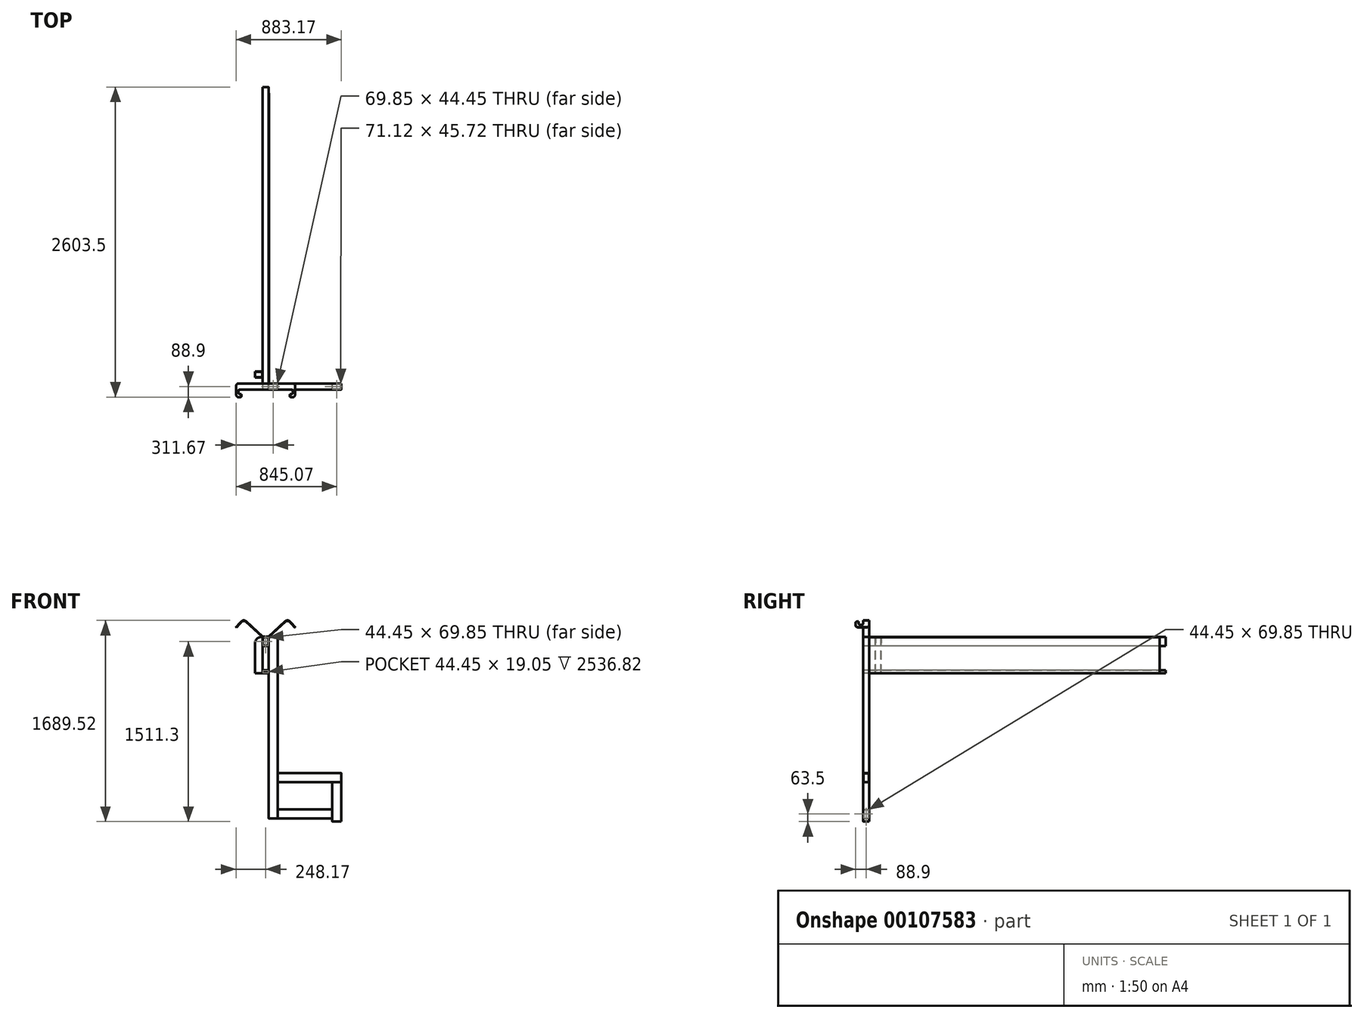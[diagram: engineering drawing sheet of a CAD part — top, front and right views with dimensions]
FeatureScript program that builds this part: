
annotation { "Feature Type Name" : "Feature", "Feature Type Description" : "" }
export const myFeature = defineFeature(function(context is Context, id is Id, definition is map)
    precondition{}
    {
        {
            var Q0;
            Q0=qCreatedBy(makeId("Right.planeOp"),FACE);
            var sketch = newSketch(context, id + "F0", { "sketchPlane" : qUnion([Q0])});
            skLineSegment(sketch, "E0.bottom", {"start": v(-25.4, 38.1) * mm, "end": v(25.4, 38.1) * mm});
            skLineSegment(sketch, "E0.top", {"start": v(-25.4, -38.1) * mm, "end": v(25.4, -38.1) * mm});
            skLineSegment(sketch, "E0.left", {"start": v(-25.4, 38.1) * mm, "end": v(-25.4, -38.1) * mm});
            skLineSegment(sketch, "E0.right", {"start": v(25.4, 38.1) * mm, "end": v(25.4, -38.1) * mm});
            skLineSegment(sketch, "E1", {"start": v(25.4, 38.1) * mm, "end": v(-25.4, -38.1) * mm, "construction": true});
            skSolve(sketch);
        }
        {
            var Q0;
            Q0=makeQuery(id+"F0.imprint","IMPRINT",FACE,{"disambiguationData":[TD([[makeQuery(id+"F0.imprint","IMPRINT",EDGE,{"derivedFrom":sQuery(id+"F0.wireOp",EDGE,"E0.bottom")}),-1.0]])]});
            extrude(context, id + "F1", {"entities" : qUnion([Q0]), "endBound" : BoundingType.SYMMETRIC, "depth" : 457.2 * mm});
        }
        {
            var Q0;
            Q0=makeQuery(id+"F1.opExtrude","SWEPT_EDGE",EDGE,{"disambiguationData":[OSD([sQuery(id+"F0.wireOp",EDGE,"E0.bottom"),sQuery(id+"F0.wireOp",EDGE,"E0.left")])]});
            var Q1;
            Q1=makeQuery(id+"F1.opExtrude","SWEPT_EDGE",EDGE,{"disambiguationData":[OSD([sQuery(id+"F0.wireOp",EDGE,"E0.bottom"),sQuery(id+"F0.wireOp",EDGE,"E0.right")])]});
            var Q2;
            Q2=makeQuery(id+"F1.opExtrude","SWEPT_EDGE",EDGE,{"disambiguationData":[OSD([sQuery(id+"F0.wireOp",EDGE,"E0.top"),sQuery(id+"F0.wireOp",EDGE,"E0.left")])]});
            var Q3;
            Q3=makeQuery(id+"F1.opExtrude","SWEPT_EDGE",EDGE,{"disambiguationData":[OSD([sQuery(id+"F0.wireOp",EDGE,"E0.top"),sQuery(id+"F0.wireOp",EDGE,"E0.right")])]});
            fillet(context, id + "F2", {"entities" : qUnion([Q0, Q1, Q2, Q3]), "radius" : 2.4 * mm, "tangentPropagation" : true, "allowEdgeOverflow" : false});
        }
        {
            var Q0;
            Q0=makeQuery(id+"F1.opExtrude","CAP_FACE",FACE,{"disambiguationData":[OSD([sQuery(id+"F0.wireOp",EDGE,"E0.bottom"),sQuery(id+"F0.wireOp",EDGE,"E0.top"),sQuery(id+"F0.wireOp",EDGE,"E0.left"),sQuery(id+"F0.wireOp",EDGE,"E0.right")])],"isStart":false});
            var Q1;
            Q1=makeQuery(id+"F1.opExtrude","CAP_FACE",FACE,{"disambiguationData":[OSD([sQuery(id+"F0.wireOp",EDGE,"E0.bottom"),sQuery(id+"F0.wireOp",EDGE,"E0.top"),sQuery(id+"F0.wireOp",EDGE,"E0.left"),sQuery(id+"F0.wireOp",EDGE,"E0.right")])],"isStart":true});
            shell(context, id + "F3", {"entities" : qUnion([Q0, Q1]), "thickness" : 3.17 * mm});
        }
        {
            var Q0;
            Q0=makeQuery(id+"F1.opExtrude","SWEPT_FACE",FACE,{"disambiguationData":[OSD([sQuery(id+"F0.wireOp",EDGE,"E0.top")])]});
            var sketch = newSketch(context, id + "F4", { "sketchPlane" : qUnion([Q0])});
            skLineSegment(sketch, "E2.bottom", {"start": v(-304.8, 25.4) * mm, "end": v(-228.6, 25.4) * mm});
            skLineSegment(sketch, "E2.top", {"start": v(-304.8, -25.4) * mm, "end": v(-228.6, -25.4) * mm});
            skLineSegment(sketch, "E2.left", {"start": v(-304.8, 25.4) * mm, "end": v(-304.8, -25.4) * mm});
            skLineSegment(sketch, "E2.right", {"start": v(-228.6, 25.4) * mm, "end": v(-228.6, -25.4) * mm});
            skSolve(sketch);
        }
        {
            var Q0;
            Q0 = qSketchRegion(id + "F4", true);
            extrude(context, id + "F5", {"entities" : qUnion([Q0]), "oppositeDirection" : true, "depth" : 1524 * mm});
        }
        {
            var Q0;
            Q0=makeQuery(id+"F5.opExtrude","SWEPT_EDGE",EDGE,{"disambiguationData":[OSD([sQuery(id+"F4.wireOp",EDGE,"E2.bottom"),sQuery(id+"F4.wireOp",EDGE,"E2.right")])]});
            var Q1;
            Q1=makeQuery(id+"F5.opExtrude","SWEPT_EDGE",EDGE,{"disambiguationData":[OSD([sQuery(id+"F4.wireOp",EDGE,"E2.top"),sQuery(id+"F4.wireOp",EDGE,"E2.right")])]});
            var Q2;
            Q2=makeQuery(id+"F5.opExtrude","SWEPT_EDGE",EDGE,{"disambiguationData":[OSD([sQuery(id+"F4.wireOp",EDGE,"E2.bottom"),sQuery(id+"F4.wireOp",EDGE,"E2.left")])]});
            var Q3;
            Q3=makeQuery(id+"F5.opExtrude","SWEPT_EDGE",EDGE,{"disambiguationData":[OSD([sQuery(id+"F4.wireOp",EDGE,"E2.top"),sQuery(id+"F4.wireOp",EDGE,"E2.left")])]});
            fillet(context, id + "F6", {"entities" : qUnion([Q0, Q1, Q2, Q3]), "radius" : 2.4 * mm, "tangentPropagation" : true, "allowEdgeOverflow" : false});
        }
        {
            var Q0;
            Q0=makeQuery(id+"F5.opExtrude","CAP_FACE",FACE,{"disambiguationData":[OSD([sQuery(id+"F4.wireOp",EDGE,"E2.bottom"),sQuery(id+"F4.wireOp",EDGE,"E2.top"),sQuery(id+"F4.wireOp",EDGE,"E2.left"),sQuery(id+"F4.wireOp",EDGE,"E2.right")])],"isStart":false});
            var Q1;
            Q1=makeQuery(id+"F5.opExtrude","CAP_FACE",FACE,{"disambiguationData":[OSD([sQuery(id+"F4.wireOp",EDGE,"E2.bottom"),sQuery(id+"F4.wireOp",EDGE,"E2.top"),sQuery(id+"F4.wireOp",EDGE,"E2.left"),sQuery(id+"F4.wireOp",EDGE,"E2.right")])],"isStart":true});
            shell(context, id + "F7", {"entities" : qUnion([Q0, Q1]), "thickness" : 3.17 * mm});
        }
        {
            var Q0;
            Q0=makeQuery(id+"F5.opExtrude","SWEPT_FACE",FACE,{"disambiguationData":[OSD([sQuery(id+"F4.wireOp",EDGE,"E2.bottom")])]});
            var sketch = newSketch(context, id + "F8", { "sketchPlane" : qUnion([Q0])});
            skLineSegment(sketch, "E3.bottom", {"start": v(-355.6, 1485.9) * mm, "end": v(-304.8, 1485.9) * mm});
            skLineSegment(sketch, "E3.top", {"start": v(-355.6, 1409.7) * mm, "end": v(-304.8, 1409.7) * mm});
            skLineSegment(sketch, "E3.left", {"start": v(-355.6, 1485.9) * mm, "end": v(-355.6, 1409.7) * mm});
            skLineSegment(sketch, "E3.right", {"start": v(-304.8, 1485.9) * mm, "end": v(-304.8, 1409.7) * mm});
            skSolve(sketch);
        }
        {
            var Q0;
            Q0=makeQuery(id+"F8.imprint","IMPRINT",FACE,{"disambiguationData":[TD([[makeQuery(id+"F8.imprint","IMPRINT",EDGE,{"derivedFrom":sQuery(id+"F8.wireOp",EDGE,"E3.bottom")}),-1.0]])]});
            extrude(context, id + "F9", {"entities" : qUnion([Q0]), "oppositeDirection" : true, "depth" : 2540 * mm});
        }
        {
            var Q0;
            Q0=makeQuery(id+"F9.opExtrude","SWEPT_EDGE",EDGE,{"disambiguationData":[OSD([sQuery(id+"F8.wireOp",EDGE,"E3.bottom"),sQuery(id+"F8.wireOp",EDGE,"E3.right")])]});
            var Q1;
            Q1=makeQuery(id+"F9.opExtrude","SWEPT_EDGE",EDGE,{"disambiguationData":[OSD([sQuery(id+"F8.wireOp",EDGE,"E3.bottom"),sQuery(id+"F8.wireOp",EDGE,"E3.left")])]});
            var Q2;
            Q2=makeQuery(id+"F9.opExtrude","SWEPT_EDGE",EDGE,{"disambiguationData":[OSD([sQuery(id+"F8.wireOp",EDGE,"E3.top"),sQuery(id+"F8.wireOp",EDGE,"E3.right")])]});
            var Q3;
            Q3=makeQuery(id+"F9.opExtrude","SWEPT_EDGE",EDGE,{"disambiguationData":[OSD([sQuery(id+"F8.wireOp",EDGE,"E3.top"),sQuery(id+"F8.wireOp",EDGE,"E3.left")])]});
            fillet(context, id + "F10", {"entities" : qUnion([Q0, Q1, Q2, Q3]), "radius" : 2.4 * mm, "tangentPropagation" : true, "allowEdgeOverflow" : false});
        }
        {
            var Q0;
            Q0=makeQuery(id+"F9.opExtrude","CAP_FACE",FACE,{"disambiguationData":[OSD([sQuery(id+"F8.wireOp",EDGE,"E3.bottom"),sQuery(id+"F8.wireOp",EDGE,"E3.top"),sQuery(id+"F8.wireOp",EDGE,"E3.left"),sQuery(id+"F8.wireOp",EDGE,"E3.right")])],"isStart":true});
            var Q1;
            Q1=makeQuery(id+"F9.opExtrude","CAP_FACE",FACE,{"disambiguationData":[OSD([sQuery(id+"F8.wireOp",EDGE,"E3.bottom"),sQuery(id+"F8.wireOp",EDGE,"E3.top"),sQuery(id+"F8.wireOp",EDGE,"E3.left"),sQuery(id+"F8.wireOp",EDGE,"E3.right")])],"isStart":false});
            shell(context, id + "F11", {"entities" : qUnion([Q0, Q1]), "thickness" : 3.17 * mm});
        }
        {
            var Q0;
            Q0=makeQuery(id+"F5.opExtrude","SWEPT_FACE",FACE,{"disambiguationData":[OSD([sQuery(id+"F4.wireOp",EDGE,"E2.bottom")])]});
            var sketch = newSketch(context, id + "F12", { "sketchPlane" : qUnion([Q0])});
            skLineSegment(sketch, "E4.bottom", {"start": v(-355.6, 1206.5) * mm, "end": v(-304.8, 1206.5) * mm});
            skLineSegment(sketch, "E4.top", {"start": v(-355.6, 1181.1) * mm, "end": v(-304.8, 1181.1) * mm});
            skLineSegment(sketch, "E4.left", {"start": v(-355.6, 1206.5) * mm, "end": v(-355.6, 1181.1) * mm});
            skLineSegment(sketch, "E4.right", {"start": v(-304.8, 1206.5) * mm, "end": v(-304.8, 1181.1) * mm});
            skSolve(sketch);
        }
        {
            var Q0;
            Q0=makeQuery(id+"F12.imprint","IMPRINT",FACE,{"disambiguationData":[TD([[makeQuery(id+"F12.imprint","IMPRINT",EDGE,{"derivedFrom":sQuery(id+"F12.wireOp",EDGE,"E4.bottom")}),-1.0]])]});
            var Q1;
            Q1=makeQuery(id+"F9.opExtrude","CAP_FACE",FACE,{"disambiguationData":[OSD([sQuery(id+"F8.wireOp",EDGE,"E3.bottom"),sQuery(id+"F8.wireOp",EDGE,"E3.top"),sQuery(id+"F8.wireOp",EDGE,"E3.left"),sQuery(id+"F8.wireOp",EDGE,"E3.right")])],"isStart":false});
            extrude(context, id + "F13", {"entities" : qUnion([Q0]), "endBound" : BoundingType.UP_TO_SURFACE, "oppositeDirection" : true, "endBoundEntityFace" : qUnion([Q1]), "depth" : 25.4 * mm});
        }
        {
            var Q0;
            Q0=makeQuery(id+"F13.opExtrude","SWEPT_EDGE",EDGE,{"disambiguationData":[OSD([sQuery(id+"F12.wireOp",EDGE,"E4.bottom"),sQuery(id+"F12.wireOp",EDGE,"E4.left")])]});
            var Q1;
            Q1=makeQuery(id+"F13.opExtrude","SWEPT_EDGE",EDGE,{"disambiguationData":[OSD([sQuery(id+"F12.wireOp",EDGE,"E4.top"),sQuery(id+"F12.wireOp",EDGE,"E4.right")])]});
            var Q2;
            Q2=makeQuery(id+"F13.opExtrude","SWEPT_EDGE",EDGE,{"disambiguationData":[OSD([sQuery(id+"F12.wireOp",EDGE,"E4.top"),sQuery(id+"F12.wireOp",EDGE,"E4.left")])]});
            fillet(context, id + "F14", {"entities" : qUnion([Q0, Q1, Q2]), "radius" : 2.4 * mm, "tangentPropagation" : true, "allowEdgeOverflow" : false});
        }
        {
            var Q0;
            Q0=makeQuery(id+"F13.opExtrude","CAP_FACE",FACE,{"disambiguationData":[OSD([sQuery(id+"F8.wireOp",EDGE,"E3.bottom"),sQuery(id+"F8.wireOp",EDGE,"E3.top"),sQuery(id+"F8.wireOp",EDGE,"E3.left"),sQuery(id+"F8.wireOp",EDGE,"E3.right")])],"isStart":false});
            var Q1;
            Q1=makeQuery(id+"F13.opExtrude","CAP_FACE",FACE,{"disambiguationData":[OSD([sQuery(id+"F12.wireOp",EDGE,"E4.bottom"),sQuery(id+"F12.wireOp",EDGE,"E4.top"),sQuery(id+"F12.wireOp",EDGE,"E4.left"),sQuery(id+"F12.wireOp",EDGE,"E4.right")])],"isStart":true});
            shell(context, id + "F15", {"entities" : qUnion([Q0, Q1]), "thickness" : 3.17 * mm});
        }
        {
            var Q0;
            Q0=makeQuery(id+"F1.opExtrude","SWEPT_FACE",FACE,{"disambiguationData":[OSD([sQuery(id+"F0.wireOp",EDGE,"E0.top")])]});
            cPlane(context, id + "F16", {"entities" : qUnion([Q0]), "cplaneType" : CPlaneType.OFFSET, "offset" : 25.4 * mm, "width" : 152.4 * mm, "height" : 152.4 * mm});
        }
        {
            var Q0;
            Q0=qCreatedBy(id+"F16.planeOp",FACE);
            var sketch = newSketch(context, id + "F17", { "sketchPlane" : qUnion([Q0])});
            skLineSegment(sketch, "E5.bottom", {"start": v(228.6, 25.4) * mm, "end": v(304.8, 25.4) * mm});
            skLineSegment(sketch, "E5.top", {"start": v(228.6, -25.4) * mm, "end": v(304.8, -25.4) * mm});
            skLineSegment(sketch, "E5.left", {"start": v(228.6, 25.4) * mm, "end": v(228.6, -25.4) * mm});
            skLineSegment(sketch, "E5.right", {"start": v(304.8, 25.4) * mm, "end": v(304.8, -25.4) * mm});
            skSolve(sketch);
        }
        {
            var Q0;
            Q0=makeQuery(id+"F17.imprint","IMPRINT",FACE,{"disambiguationData":[TD([[makeQuery(id+"F17.imprint","IMPRINT",EDGE,{"derivedFrom":sQuery(id+"F17.wireOp",EDGE,"E5.bottom")}),-1.0]])]});
            extrude(context, id + "F18", {"entities" : qUnion([Q0]), "oppositeDirection" : true, "depth" : 330.2 * mm});
        }
        {
            var Q0;
            Q0=makeQuery(id+"F18.opExtrude","SWEPT_EDGE",EDGE,{"disambiguationData":[OSD([sQuery(id+"F17.wireOp",EDGE,"E5.bottom"),sQuery(id+"F17.wireOp",EDGE,"E5.left")])]});
            var Q1;
            Q1=makeQuery(id+"F18.opExtrude","SWEPT_EDGE",EDGE,{"disambiguationData":[OSD([sQuery(id+"F17.wireOp",EDGE,"E5.bottom"),sQuery(id+"F17.wireOp",EDGE,"E5.right")])]});
            var Q2;
            Q2=makeQuery(id+"F18.opExtrude","SWEPT_EDGE",EDGE,{"disambiguationData":[OSD([sQuery(id+"F17.wireOp",EDGE,"E5.top"),sQuery(id+"F17.wireOp",EDGE,"E5.right")])]});
            var Q3;
            Q3=makeQuery(id+"F18.opExtrude","SWEPT_EDGE",EDGE,{"disambiguationData":[OSD([sQuery(id+"F17.wireOp",EDGE,"E5.top"),sQuery(id+"F17.wireOp",EDGE,"E5.left")])]});
            fillet(context, id + "F19", {"entities" : qUnion([Q0, Q1, Q2, Q3]), "radius" : 2.4 * mm, "tangentPropagation" : true, "allowEdgeOverflow" : false});
        }
        {
            var Q0;
            Q0=makeQuery(id+"F18.opExtrude","CAP_FACE",FACE,{"disambiguationData":[OSD([sQuery(id+"F17.wireOp",EDGE,"E5.bottom"),sQuery(id+"F17.wireOp",EDGE,"E5.top"),sQuery(id+"F17.wireOp",EDGE,"E5.left"),sQuery(id+"F17.wireOp",EDGE,"E5.right")])],"isStart":false});
            var Q1;
            Q1=makeQuery(id+"F18.opExtrude","CAP_FACE",FACE,{"disambiguationData":[OSD([sQuery(id+"F17.wireOp",EDGE,"E5.bottom"),sQuery(id+"F17.wireOp",EDGE,"E5.top"),sQuery(id+"F17.wireOp",EDGE,"E5.left"),sQuery(id+"F17.wireOp",EDGE,"E5.right")])],"isStart":true});
            shell(context, id + "F20", {"entities" : qUnion([Q0, Q1]), "thickness" : 2.54 * mm});
        }
        {
            var Q0;
            Q0=makeQuery(id+"F18.opExtrude","SWEPT_FACE",FACE,{"disambiguationData":[OSD([sQuery(id+"F17.wireOp",EDGE,"E5.right")])]});
            var sketch = newSketch(context, id + "F21", { "sketchPlane" : qUnion([Q0])});
            skLineSegment(sketch, "E6.bottom", {"start": v(-25.4, 342.9) * mm, "end": v(25.4, 342.9) * mm});
            skLineSegment(sketch, "E6.top", {"start": v(-25.4, 266.7) * mm, "end": v(25.4, 266.7) * mm});
            skLineSegment(sketch, "E6.left", {"start": v(-25.4, 342.9) * mm, "end": v(-25.4, 266.7) * mm});
            skLineSegment(sketch, "E6.right", {"start": v(25.4, 342.9) * mm, "end": v(25.4, 266.7) * mm});
            skSolve(sketch);
        }
        {
            var Q0;
            Q0=makeQuery(id+"F21.imprint","IMPRINT",FACE,{"disambiguationData":[TD([[makeQuery(id+"F21.imprint","IMPRINT",EDGE,{"derivedFrom":sQuery(id+"F21.wireOp",EDGE,"E6.bottom")}),-1.0]])]});
            var Q1;
            Q1=makeQuery(id+"F5.opExtrude","SWEPT_FACE",FACE,{"disambiguationData":[OSD([sQuery(id+"F4.wireOp",EDGE,"E2.right")])]});
            extrude(context, id + "F22", {"entities" : qUnion([Q0]), "endBound" : BoundingType.UP_TO_SURFACE, "oppositeDirection" : true, "endBoundEntityFace" : qUnion([Q1]), "depth" : 25.4 * mm});
        }
        {
            var Q0;
            Q0=makeQuery(id+"F22.opExtrude","SWEPT_EDGE",EDGE,{"disambiguationData":[OSD([sQuery(id+"F21.wireOp",EDGE,"E6.bottom"),sQuery(id+"F21.wireOp",EDGE,"E6.left")])]});
            fillet(context, id + "F23", {"entities" : qUnion([Q0]), "radius" : 5.08 * mm, "tangentPropagation" : true, "allowEdgeOverflow" : false});
        }
        {
            var Q0;
            Q0=makeQuery(id+"F22.opExtrude","CAP_FACE",FACE,{"disambiguationData":[OSD([sQuery(id+"F21.wireOp",EDGE,"E6.bottom"),sQuery(id+"F21.wireOp",EDGE,"E6.top"),sQuery(id+"F21.wireOp",EDGE,"E6.left"),sQuery(id+"F21.wireOp",EDGE,"E6.right")])],"isStart":true});
            var Q1;
            Q1=makeQuery(id+"F22.opExtrude","CAP_FACE",FACE,{"disambiguationData":[OSD([sQuery(id+"F4.wireOp",EDGE,"E2.right")])],"isStart":false});
            shell(context, id + "F24", {"entities" : qUnion([Q0, Q1]), "thickness" : 2.54 * mm});
        }
        {
            var Q0;
            Q0=makeQuery(id+"F9.opExtrude","SWEPT_FACE",FACE,{"disambiguationData":[OSD([sQuery(id+"F8.wireOp",EDGE,"E3.right")])]});
            var sketch = newSketch(context, id + "F25", { "sketchPlane" : qUnion([Q0])});
            skLineSegment(sketch, "E7.bottom", {"start": v(25.4, 1485.9) * mm, "end": v(2463.8, 1485.9) * mm});
            skLineSegment(sketch, "E7.top", {"start": v(25.4, 1181.1) * mm, "end": v(2463.8, 1181.1) * mm});
            skLineSegment(sketch, "E7.left", {"start": v(25.4, 1485.9) * mm, "end": v(25.4, 1181.1) * mm});
            skLineSegment(sketch, "E7.right", {"start": v(2463.8, 1485.9) * mm, "end": v(2463.8, 1181.1) * mm});
            skSolve(sketch);
        }
        {
            var Q0;
            {var subQ0=sQuery(id+"F25.wireOp",EDGE,"E7.top");Q0=makeQuery(id+"F25.imprint","IMPRINT",FACE,{"disambiguationData":[TD([[makeQuery(id+"F25.imprint","IMPRINT",EDGE,{"derivedFrom":subQ0}),1.0]])]});}
            var Q1;
            {var subQ0=sQuery(id+"F25.wireOp",EDGE,"E7.left");var subQ1=sQuery(id+"F8.wireOp",EDGE,"E3.right");var subQ2=makeQuery(id+"F9.opExtrude","SWEPT_FACE",FACE,{"disambiguationData":[OSD([subQ1])]});var subQ3=makeQuery(id+"F10.opFillet","BLEND_EDGE",EDGE,{"blendedFrom":[makeQuery(id+"F9.opExtrude","SWEPT_EDGE",EDGE,{"disambiguationData":[OSD([sQuery(id+"F8.wireOp",EDGE,"E3.bottom"),subQ1])]}),subQ2],"blendedInto":[subQ2]});var subQ4=makeQuery(id+"F25.imprint","INTERSECT",VERTEX,{"derivedFrom":[subQ3,subQ0]});Q1=makeQuery(id+"F25.imprint","IMPRINT",FACE,{"disambiguationData":[TD([[makeQuery(id+"F25.imprint","IMPRINT",EDGE,{"disambiguationData":[TD([[subQ4,-1.0]])],"derivedFrom":subQ0}),1.0]])]});}
            extrude(context, id + "F26", {"entities" : qUnion([Q0, Q1]), "depth" : 3.17 * mm});
        }
        {
            var Q0;
            Q0=makeQuery(id+"F5.opExtrude","SWEPT_FACE",FACE,{"disambiguationData":[OSD([sQuery(id+"F4.wireOp",EDGE,"E2.bottom")])]});
            var sketch = newSketch(context, id + "F27", { "sketchPlane" : qUnion([Q0])});
            skLineSegment(sketch, "E8.0", {"start": v(-301.63, 1483.51) * mm, "end": v(-301.63, 1181.1) * mm, "construction": true});
            skLineSegment(sketch, "E9", {"start": v(-301.63, 1332.3) * mm, "end": v(53.98, 1332.3) * mm, "construction": true});
            skCircle(sketch, "E10", {"center": v(53.98, 1332.3) * mm, "radius": 355.6 * mm, "construction": true});
            skCircle(sketch, "E11.0", {"center": v(53.98, 1332.3) * mm, "radius": 317.5 * mm, "construction": true});
            skLineSegment(sketch, "E12", {"start": v(-330.2, 1485.9) * mm, "end": v(-304.8, 1485.9) * mm});
            skLineSegment(sketch, "E13", {"start": v(-304.8, 1485.9) * mm, "end": v(-145.6, 1631.73) * mm});
            skLineSegment(sketch, "E14", {"start": v(-145.6, 1631.73) * mm, "end": v(-85.55, 1566.18) * mm});
            skLineSegment(sketch, "E15.0", {"start": v(-353.21, 1485.9) * mm, "end": v(-307.19, 1485.9) * mm, "construction": true});
            skLineSegment(sketch, "E16.0", {"start": v(-353.21, 1409.7) * mm, "end": v(-307.19, 1409.7) * mm, "construction": true});
            skLineSegment(sketch, "E17", {"start": v(-330.2, 1485.9) * mm, "end": v(-330.2, 1409.7) * mm, "construction": true});
            skLineSegment(sketch, "E18.0", {"start": v(-145.3, 1638.48) * mm, "end": v(-82.03, 1569.4) * mm});
            skLineSegment(sketch, "E18.1", {"start": v(-306.66, 1490.68) * mm, "end": v(-145.3, 1638.48) * mm});
            skLineSegment(sketch, "E18.2", {"start": v(-330.2, 1490.68) * mm, "end": v(-306.66, 1490.68) * mm});
            skLineSegment(sketch, "E19", {"start": v(-82.03, 1569.4) * mm, "end": v(-85.55, 1566.18) * mm});
            skLineSegment(sketch, "E20", {"start": v(-330.2, 1490.68) * mm, "end": v(-330.2, 1485.9) * mm});
            skSolve(sketch);
        }
        {
            var Q0;
            Q0=makeQuery(id+"F27.imprint","IMPRINT",FACE,{"disambiguationData":[TD([[makeQuery(id+"F27.imprint","IMPRINT",EDGE,{"derivedFrom":sQuery(id+"F27.wireOp",EDGE,"E12")}),1.0]])]});
            extrude(context, id + "F28", {"entities" : qUnion([Q0]), "oppositeDirection" : true, "depth" : 50.8 * mm});
        }
        {
            var Q0;
            Q0=makeQuery(id+"F27.imprint","IMPRINT",FACE,{"disambiguationData":[TD([[makeQuery(id+"F27.imprint","IMPRINT",EDGE,{"derivedFrom":sQuery(id+"F27.wireOp",EDGE,"E12")}),1.0]])]});
            var sketch = newSketch(context, id + "F29", { "sketchPlane" : qUnion([Q0])});
            skLineSegment(sketch, "E21", {"start": v(-128.44, 1613) * mm, "end": v(-124.92, 1616.23) * mm});
            skLineSegment(sketch, "E22", {"start": v(-124.92, 1616.23) * mm, "end": v(-82.03, 1569.4) * mm});
            skLineSegment(sketch, "E23", {"start": v(-82.03, 1569.4) * mm, "end": v(-85.55, 1566.18) * mm});
            skLineSegment(sketch, "E24", {"start": v(-85.55, 1566.18) * mm, "end": v(-128.44, 1613) * mm});
            skSolve(sketch);
        }
        {
            var Q0;
            Q0=makeQuery(id+"F29.imprint","IMPRINT",FACE,{"disambiguationData":[TD([[makeQuery(id+"F29.imprint","IMPRINT",EDGE,{"derivedFrom":sQuery(id+"F29.wireOp",EDGE,"E21")}),-1.0]])]});
            extrude(context, id + "F30", {"entities" : qUnion([Q0]), "operationType" : NewBodyOperationType.ADD, "depth" : 63.5 * mm});
        }
        {
            var Q0;
            Q0=makeQuery(id+"F30.boolean.opBoolean","MERGE",FACE,{"derivedFrom":[makeQuery(id+"F28.opExtrude","SWEPT_FACE",FACE,{"disambiguationData":[OSD([sQuery(id+"F27.wireOp",EDGE,"E18.0")])]}),makeQuery(id+"F30.opExtrude","SWEPT_FACE",FACE,{"disambiguationData":[OSD([sQuery(id+"F29.wireOp",EDGE,"E22")])]})]});
            var sketch = newSketch(context, id + "F31", { "sketchPlane" : qUnion([Q0])});
            skLineSegment(sketch, "E25", {"start": v(-25.4, 1276.17) * mm, "end": v(-25.4, 1257.12) * mm});
            skArc(sketch, "E26", {"start": v(-63.5, 1257.12) * mm, "mid": v(-44.45, 1238.07) * mm, "end": v(-25.4, 1257.12) * mm});
            skLineSegment(sketch, "E27", {"start": v(-63.5, 1257.12) * mm, "end": v(-63.5, 1276.17) * mm});
            skSolve(sketch);
        }
        {
            var Q0;
            Q0 = qSketchRegion(id + "F31", true);
            var Q1;
            {var subQ0=sQuery(id+"F31.wireOp",EDGE,"E25");Q1=makeQuery(id+"F31.imprint","IMPRINT",FACE,{"disambiguationData":[TD([[makeQuery(id+"F31.imprint","IMPRINT",EDGE,{"derivedFrom":subQ0}),-1.0]])]});}
            extrude(context, id + "F32", {"entities" : qUnion([Q0, Q1]), "operationType" : NewBodyOperationType.REMOVE, "endBound" : BoundingType.THROUGH_ALL, "oppositeDirection" : true, "depth" : 25.4 * mm});
        }
        {
            var Q0;
            Q0=makeQuery(id+"F28.opExtrude","SWEPT_EDGE",EDGE,{"disambiguationData":[OSD([sQuery(id+"F27.wireOp",EDGE,"E18.1"),sQuery(id+"F27.wireOp",EDGE,"E18.2")])]});
            fillet(context, id + "F33", {"entities" : qUnion([Q0]), "radius" : 3.17 * mm, "tangentPropagation" : true, "allowEdgeOverflow" : false});
        }
        {
            var Q0;
            Q0=makeQuery(id+"F28.opExtrude","SWEPT_EDGE",EDGE,{"disambiguationData":[OSD([sQuery(id+"F27.wireOp",EDGE,"E12"),sQuery(id+"F27.wireOp",EDGE,"E13")])]});
            fillet(context, id + "F34", {"entities" : qUnion([Q0]), "radius" : 4.78 * mm, "tangentPropagation" : true, "allowEdgeOverflow" : false});
        }
        {
            var Q0;
            Q0=makeQuery(id+"F28.opExtrude","SWEPT_EDGE",EDGE,{"disambiguationData":[OSD([sQuery(id+"F27.wireOp",EDGE,"E13"),sQuery(id+"F27.wireOp",EDGE,"E14")])]});
            fillet(context, id + "F35", {"entities" : qUnion([Q0]), "radius" : 25.4 * mm, "tangentPropagation" : true, "allowEdgeOverflow" : false});
        }
        {
            var Q0;
            Q0=makeQuery(id+"F28.opExtrude","SWEPT_EDGE",EDGE,{"disambiguationData":[OSD([sQuery(id+"F27.wireOp",EDGE,"E18.0"),sQuery(id+"F27.wireOp",EDGE,"E18.1")])]});
            fillet(context, id + "F36", {"entities" : qUnion([Q0]), "radius" : 30.18 * mm, "tangentPropagation" : true, "allowEdgeOverflow" : false});
        }
        {
            var Q0;
            Q0=makeQuery(id+"F28.opExtrude","CAP_EDGE",EDGE,{"disambiguationData":[OSD([sQuery(id+"F27.wireOp",EDGE,"E19")])],"isStart":false});
            var Q1;
            Q1=makeQuery(id+"F30.opExtrude","CAP_EDGE",EDGE,{"disambiguationData":[OSD([sQuery(id+"F29.wireOp",EDGE,"E23")])],"isStart":false});
            fillet(context, id + "F37", {"entities" : qUnion([Q0, Q1]), "radius" : 25.4 * mm, "tangentPropagation" : true, "allowEdgeOverflow" : false});
        }
        {
            var Q0;
            Q0=makeQuery(id+"F30.opExtrude","CAP_EDGE",EDGE,{"disambiguationData":[OSD([sQuery(id+"F29.wireOp",EDGE,"E21")])],"isStart":false});
            var Q1;
            Q1=makeQuery(id+"F32.boolean.opBoolean","COPY",EDGE,{"derivedFrom":makeQuery(id+"F32.opExtrude","SWEPT_EDGE",EDGE,{"disambiguationData":[OSD([sQuery(id+"F27.wireOp",EDGE,"E18.0"),sQuery(id+"F29.wireOp",EDGE,"E21"),sQuery(id+"F29.wireOp",EDGE,"E22"),sQuery(id+"F31.wireOp",EDGE,"E27")])]})});
            fillet(context, id + "F38", {"entities" : qUnion([Q0, Q1]), "radius" : 12.7 * mm, "tangentPropagation" : true, "allowEdgeOverflow" : false});
        }
        {
            var Q0;
            Q0=makeQuery(id+"F28.opExtrude","SWEPT_FACE",FACE,{"disambiguationData":[OSD([sQuery(id+"F27.wireOp",EDGE,"E20")])]});
            cPlane(context, id + "F39", {"entities" : qUnion([Q0]), "cplaneType" : CPlaneType.OFFSET, "offset" : 0 * mm, "width" : 152.4 * mm, "height" : 152.4 * mm});
        }
        {
            var Q0;
            Q0=makeQuery(id+"F28.opExtrude","SWEPT_BODY",BODY,{"disambiguationData":[OSD([sQuery(id+"F27.wireOp",EDGE,"E12"),sQuery(id+"F27.wireOp",EDGE,"E13"),sQuery(id+"F27.wireOp",EDGE,"E14"),sQuery(id+"F27.wireOp",EDGE,"E18.0"),sQuery(id+"F27.wireOp",EDGE,"E18.1"),sQuery(id+"F27.wireOp",EDGE,"E18.2"),sQuery(id+"F27.wireOp",EDGE,"E19"),sQuery(id+"F27.wireOp",EDGE,"E20")])]});
            var Q1;
            Q1=qCreatedBy(id+"F39.planeOp",FACE);
            mirror(context, id + "F40", {"operationType" : NewBodyOperationType.ADD, "entities" : qUnion([Q0]), "mirrorPlane" : qUnion([Q1])});
        }
        {
            var Q0;
            Q0=makeQuery(id+"F9.opExtrude","SWEPT_FACE",FACE,{"disambiguationData":[OSD([sQuery(id+"F8.wireOp",EDGE,"E3.bottom")])]});
            var sketch = newSketch(context, id + "F41", { "sketchPlane" : qUnion([Q0])});
            skLineSegment(sketch, "E28.bottom", {"start": v(-419.1, 76.2) * mm, "end": v(-355.6, 76.2) * mm});
            skLineSegment(sketch, "E28.top", {"start": v(-419.1, 127) * mm, "end": v(-355.6, 127) * mm});
            skLineSegment(sketch, "E28.left", {"start": v(-419.1, 127) * mm, "end": v(-419.1, 76.2) * mm});
            skLineSegment(sketch, "E28.right", {"start": v(-355.6, 127) * mm, "end": v(-355.6, 76.2) * mm});
            skSolve(sketch);
        }
        {
            var Q0;
            Q0=makeQuery(id+"F41.imprint","IMPRINT",FACE,{"disambiguationData":[TD([[makeQuery(id+"F41.imprint","IMPRINT",EDGE,{"derivedFrom":sQuery(id+"F41.wireOp",EDGE,"E28.bottom")}),1.0]])]});
            var Q1;
            Q1=makeQuery(id+"F13.opExtrude","SWEPT_FACE",FACE,{"disambiguationData":[OSD([sQuery(id+"F12.wireOp",EDGE,"E4.top")])]});
            extrude(context, id + "F42", {"entities" : qUnion([Q0]), "endBound" : BoundingType.UP_TO_SURFACE, "oppositeDirection" : true, "endBoundEntityFace" : qUnion([Q1]), "depth" : 25.4 * mm});
        }
        {
            var Q0;
            Q0=makeQuery(id+"F42.opExtrude","TWEAK_EDGE",EDGE,{"derivedFrom":[makeQuery(id+"F13.opExtrude","SWEPT_FACE",FACE,{"disambiguationData":[OSD([sQuery(id+"F12.wireOp",EDGE,"E4.top")])]}),makeQuery(id+"F41.imprint","IMPRINT",EDGE,{"derivedFrom":sQuery(id+"F41.wireOp",EDGE,"E28.left")})]});
            var Q1;
            Q1=makeQuery(id+"F42.opExtrude","CAP_EDGE",EDGE,{"disambiguationData":[OSD([sQuery(id+"F41.wireOp",EDGE,"E28.left")])],"isStart":true});
            fillet(context, id + "F43", {"entities" : qUnion([Q0, Q1]), "radius" : 50.8 * mm, "tangentPropagation" : true, "allowEdgeOverflow" : false});
        }
        {
            var Q0;
            Q0=makeQuery(id+"F42.opExtrude","SWEPT_FACE",FACE,{"disambiguationData":[OSD([sQuery(id+"F41.wireOp",EDGE,"E28.left")])]});
            var Q1;
            Q1=makeQuery(id+"F43.opFillet","BLEND_FACE",FACE,{"disambiguationData":[OSD([sQuery(id+"F12.wireOp",EDGE,"E4.top"),sQuery(id+"F41.wireOp",EDGE,"E28.left")])]});
            var Q2;
            Q2=makeQuery(id+"F42.opExtrude","CAP_FACE",FACE,{"disambiguationData":[OSD([sQuery(id+"F12.wireOp",EDGE,"E4.top")])],"isStart":false});
            var Q3;
            Q3=makeQuery(id+"F43.opFillet","BLEND_FACE",FACE,{"disambiguationData":[OSD([sQuery(id+"F41.wireOp",EDGE,"E28.left")])]});
            var Q4;
            Q4=makeQuery(id+"F42.opExtrude","CAP_FACE",FACE,{"disambiguationData":[OSD([sQuery(id+"F41.wireOp",EDGE,"E28.bottom"),sQuery(id+"F41.wireOp",EDGE,"E28.top"),sQuery(id+"F41.wireOp",EDGE,"E28.left"),sQuery(id+"F41.wireOp",EDGE,"E28.right")])],"isStart":true});
            shell(context, id + "F44", {"entities" : qUnion([Q0, Q1, Q2, Q3, Q4]), "thickness" : 3.17 * mm});
        }
    });
